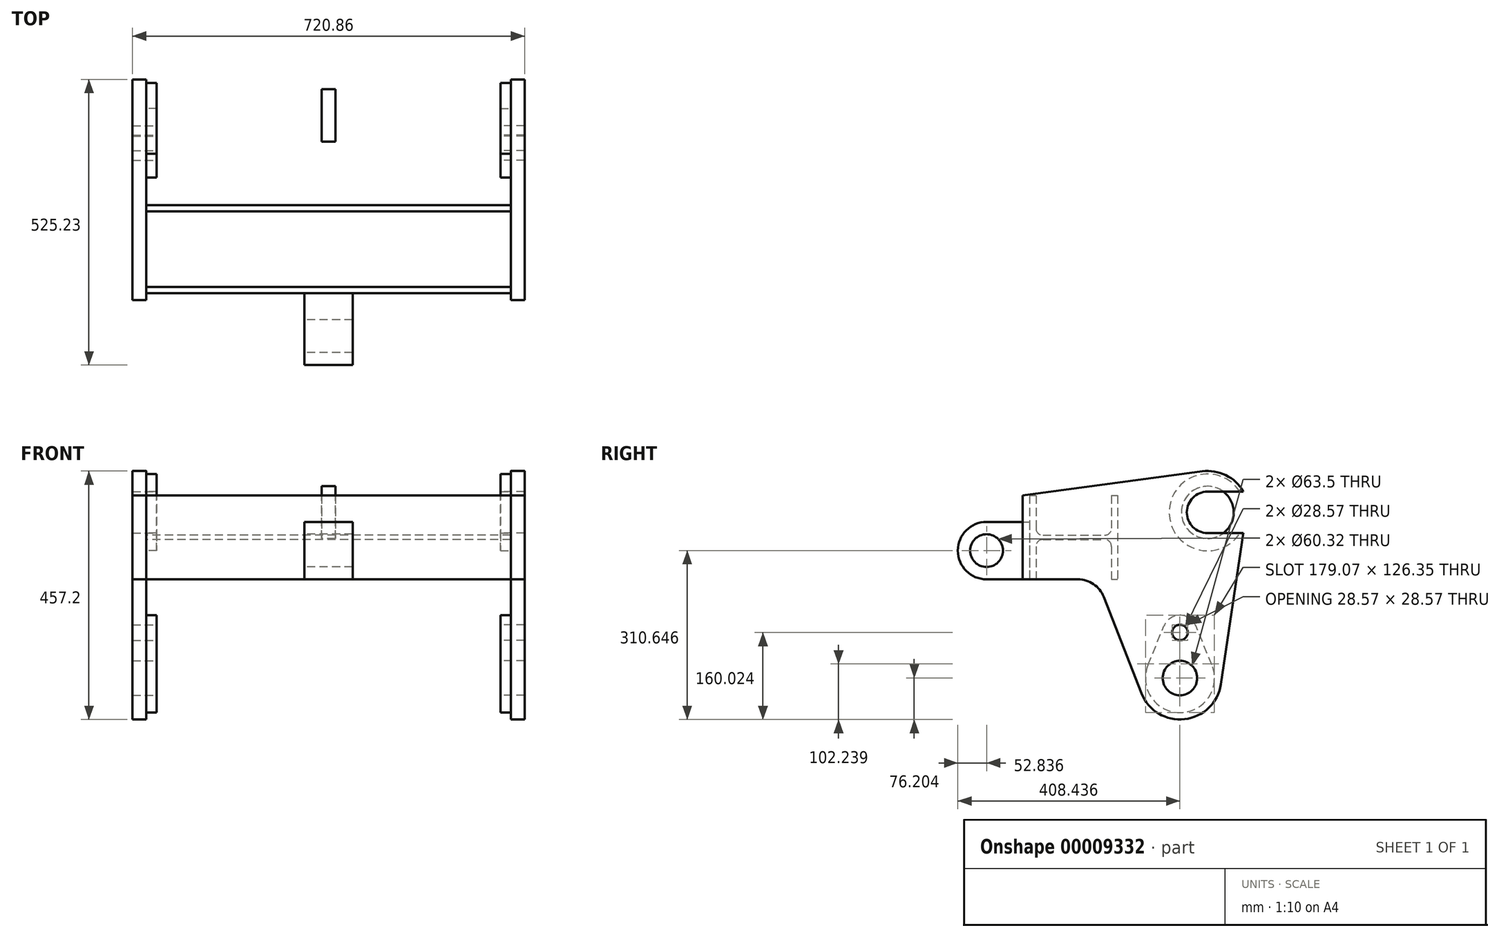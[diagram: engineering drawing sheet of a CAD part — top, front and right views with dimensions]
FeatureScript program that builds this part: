
annotation { "Feature Type Name" : "Feature", "Feature Type Description" : "" }
export const myFeature = defineFeature(function(context is Context, id is Id, definition is map)
    precondition{}
    {
        {
            var Q0;
            Q0=qCreatedBy(makeId("Right.planeOp"),FACE);
            var sketch = newSketch(context, id + "F0", { "sketchPlane" : qUnion([Q0])});
            skLineSegment(sketch, "E0.rect.bottom", {"start": v(-81.03, 77.22) * mm, "end": v(-69.47, 77.22) * mm});
            skLineSegment(sketch, "E0.rect.top", {"start": v(-81.03, -77.22) * mm, "end": v(-69.47, -77.22) * mm});
            skLineSegment(sketch, "E0.rect.left", {"start": v(-81.03, 77.22) * mm, "end": v(-81.03, -77.22) * mm});
            skLineSegment(sketch, "E0.rect.right", {"start": v(81.03, 77.22) * mm, "end": v(81.03, -77.22) * mm});
            skPoint(sketch, "E0.rect.middle", {"position": v(0, 0) * mm});
            skLineSegment(sketch, "E1.0", {"start": v(-69.47, 77.22) * mm, "end": v(-69.47, -77.22) * mm});
            skLineSegment(sketch, "E2", {"start": v(-81.03, 0) * mm, "end": v(81.03, 0) * mm, "construction": true});
            skLineSegment(sketch, "E3", {"start": v(0, 77.22) * mm, "end": v(0, -77.22) * mm, "construction": true});
            skLineSegment(sketch, "E4.0", {"start": v(-81.03, -4.06) * mm, "end": v(81.03, -4.06) * mm});
            skLineSegment(sketch, "E5.0.MirrorCS", {"start": v(-81.03, 4.06) * mm, "end": v(81.03, 4.06) * mm});
            skLineSegment(sketch, "E6.0.MirrorCS", {"start": v(69.47, 77.22) * mm, "end": v(69.47, -77.22) * mm});
            skLineSegment(sketch, "E7.trimOffspring", {"start": v(69.47, 77.22) * mm, "end": v(81.03, 77.22) * mm});
            skLineSegment(sketch, "E8.trimOffspring", {"start": v(69.47, -77.22) * mm, "end": v(81.03, -77.22) * mm});
            skSolve(sketch);
        }
        {
            var Q0;
            Q0 = qSketchRegion(id + "F0", true);
            extrude(context, id + "F1", {"entities" : qUnion([Q0]), "endBound" : BoundingType.SYMMETRIC, "depth" : 670.05 * mm});
        }
        {
            var Q0;
            Q0=makeQuery(id+"F1.opExtrude","SWEPT_EDGE",EDGE,{"disambiguationData":[OSD([sQuery(id+"F0.wireOp",EDGE,"E5.0.MirrorCS"),sQuery(id+"F0.wireOp",EDGE,"E6.0.MirrorCS")])]});
            var Q1;
            Q1=makeQuery(id+"F1.opExtrude","SWEPT_EDGE",EDGE,{"disambiguationData":[OSD([sQuery(id+"F0.wireOp",EDGE,"E4.0"),sQuery(id+"F0.wireOp",EDGE,"E6.0.MirrorCS")])]});
            var Q2;
            Q2=makeQuery(id+"F1.opExtrude","SWEPT_EDGE",EDGE,{"disambiguationData":[OSD([sQuery(id+"F0.wireOp",EDGE,"E1.0"),sQuery(id+"F0.wireOp",EDGE,"E5.0.MirrorCS")])]});
            var Q3;
            Q3=makeQuery(id+"F1.opExtrude","SWEPT_EDGE",EDGE,{"disambiguationData":[OSD([sQuery(id+"F0.wireOp",EDGE,"E1.0"),sQuery(id+"F0.wireOp",EDGE,"E4.0")])]});
            fillet(context, id + "F2", {"entities" : qUnion([Q0, Q1, Q2, Q3]), "radius" : 12.7 * mm, "tangentPropagation" : true, "allowEdgeOverflow" : false});
        }
        {
            var Q0;
            Q0=makeQuery(id+"F1.opExtrude","CAP_FACE",FACE,{"disambiguationData":[OSD([sQuery(id+"F0.wireOp",EDGE,"E0.rect.bottom"),sQuery(id+"F0.wireOp",EDGE,"E0.rect.top"),sQuery(id+"F0.wireOp",EDGE,"E0.rect.left"),sQuery(id+"F0.wireOp",EDGE,"E0.rect.right"),sQuery(id+"F0.wireOp",EDGE,"E1.0"),sQuery(id+"F0.wireOp",EDGE,"E4.0"),sQuery(id+"F0.wireOp",EDGE,"E5.0.MirrorCS"),sQuery(id+"F0.wireOp",EDGE,"E6.0.MirrorCS"),sQuery(id+"F0.wireOp",EDGE,"E7.trimOffspring"),sQuery(id+"F0.wireOp",EDGE,"E8.trimOffspring")])],"isStart":false});
            var sketch = newSketch(context, id + "F3", { "sketchPlane" : qUnion([Q0])});
            skLineSegment(sketch, "E9", {"start": v(-81.03, -4.06) * mm, "end": v(-81.03, 203.68) * mm, "construction": true});
            skLineSegment(sketch, "E10.0", {"start": v(246.13, -4.06) * mm, "end": v(246.13, 203.68) * mm, "construction": true});
            skLineSegment(sketch, "E11", {"start": v(81.03, 0) * mm, "end": v(356.17, 0) * mm, "construction": true});
            skLineSegment(sketch, "E12.0", {"start": v(81.03, 45.97) * mm, "end": v(356.17, 45.97) * mm, "construction": true});
            skArc(sketch, "E13", {"start": v(312.12, 84.07) * mm, "mid": v(279.74, 114.36) * mm, "end": v(235.98, 121.5) * mm});
            skArc(sketch, "E14", {"start": v(246.13, 84.07) * mm, "mid": v(208.03, 45.97) * mm, "end": v(246.13, 7.87) * mm});
            skLineSegment(sketch, "E15", {"start": v(246.13, 84.07) * mm, "end": v(312.12, 84.07) * mm});
            skLineSegment(sketch, "E16", {"start": v(246.13, 7.87) * mm, "end": v(312.12, 7.87) * mm});
            skLineSegment(sketch, "E17.0", {"start": v(81.03, -258.83) * mm, "end": v(356.17, -258.83) * mm, "construction": true});
            skLineSegment(sketch, "E18.0", {"start": v(195.33, -258.83) * mm, "end": v(195.33, 203.68) * mm, "construction": true});
            skCircle(sketch, "E19", {"center": v(195.33, -258.83) * mm, "radius": 31.75 * mm});
            skArc(sketch, "E20", {"start": v(124.35, -286.55) * mm, "mid": v(209.43, -333.7) * mm, "end": v(271.53, -258.83) * mm});
            skLineSegment(sketch, "E21.0", {"start": v(-93.73, 77.22) * mm, "end": v(-93.73, -77.22) * mm});
            skLineSegment(sketch, "E22", {"start": v(-93.73, 77.22) * mm, "end": v(235.98, 121.5) * mm});
            skLineSegment(sketch, "E23.0", {"start": v(7.87, 77.22) * mm, "end": v(7.87, -128.02) * mm, "construction": true});
            skLineSegment(sketch, "E24", {"start": v(-93.73, -77.22) * mm, "end": v(7.87, -77.22) * mm});
            skLineSegment(sketch, "E25.0", {"start": v(-93.73, -128.02) * mm, "end": v(133.5, -128.02) * mm, "construction": true});
            skArc(sketch, "E26", {"start": v(55.2, -109.53) * mm, "mid": v(36.52, -86.07) * mm, "end": v(7.87, -77.22) * mm});
            skLineSegment(sketch, "E27.trimOffspring", {"start": v(113.52, -258.83) * mm, "end": v(124.35, -286.55) * mm});
            skLineSegment(sketch, "E28", {"start": v(113.52, -258.83) * mm, "end": v(55.2, -109.53) * mm});
            skLineSegment(sketch, "E29", {"start": v(312.12, 7.87) * mm, "end": v(270.7, -270.06) * mm});
            skSolve(sketch);
        }
        {
            var Q0;
            Q0 = qSketchRegion(id + "F3", true);
            extrude(context, id + "F4", {"entities" : qUnion([Q0]), "operationType" : NewBodyOperationType.ADD, "depth" : 25.4 * mm});
        }
        {
            var Q0;
            Q0=makeQuery(id+"F4.opExtrude","CAP_FACE",FACE,{"disambiguationData":[OSD([sQuery(id+"F3.wireOp",EDGE,"E13"),sQuery(id+"F3.wireOp",EDGE,"E14"),sQuery(id+"F3.wireOp",EDGE,"E15"),sQuery(id+"F3.wireOp",EDGE,"E16"),sQuery(id+"F3.wireOp",EDGE,"E19"),sQuery(id+"F3.wireOp",EDGE,"E20"),sQuery(id+"F3.wireOp",EDGE,"E21.0"),sQuery(id+"F3.wireOp",EDGE,"E22"),sQuery(id+"F3.wireOp",EDGE,"E24"),sQuery(id+"F3.wireOp",EDGE,"E26"),sQuery(id+"F3.wireOp",EDGE,"E27.trimOffspring"),sQuery(id+"F3.wireOp",EDGE,"E28"),sQuery(id+"F3.wireOp",EDGE,"E29")])],"isStart":true});
            var sketch = newSketch(context, id + "F5", { "sketchPlane" : qUnion([Q0])});
            skArc(sketch, "E30", {"start": v(-254.1, -234.77) * mm, "mid": v(-195.33, -322.33) * mm, "end": v(-136.56, -234.77) * mm});
            skLineSegment(sketch, "E31", {"start": v(-195.33, -258.83) * mm, "end": v(-195.33, -175) * mm, "construction": true});
            skArc(sketch, "E32", {"start": v(-165.94, -162.98) * mm, "mid": v(-195.33, -143.26) * mm, "end": v(-224.71, -162.98) * mm});
            skCircle(sketch, "E33.0", {"center": v(-195.33, -258.83) * mm, "radius": 31.75 * mm});
            skLineSegment(sketch, "E34", {"start": v(-254.1, -234.77) * mm, "end": v(-224.71, -162.98) * mm});
            skLineSegment(sketch, "E35.0.MirrorCS", {"start": v(-136.56, -234.77) * mm, "end": v(-165.94, -162.98) * mm});
            skSolve(sketch);
        }
        {
            var Q0;
            Q0 = qSketchRegion(id + "F5", true);
            extrude(context, id + "F6", {"entities" : qUnion([Q0]), "operationType" : NewBodyOperationType.ADD, "depth" : 19.05 * mm});
        }
        {
            var Q0;
            Q0=makeQuery(id+"F6.opExtrude","CAP_FACE",FACE,{"disambiguationData":[OSD([sQuery(id+"F5.wireOp",EDGE,"E30"),sQuery(id+"F5.wireOp",EDGE,"E32"),sQuery(id+"F5.wireOp",EDGE,"E33.0"),sQuery(id+"F5.wireOp",EDGE,"E34"),sQuery(id+"F5.wireOp",EDGE,"E35.0.MirrorCS")])],"isStart":false});
            var sketch = newSketch(context, id + "F7", { "sketchPlane" : qUnion([Q0])});
            skCircle(sketch, "E36", {"center": v(-195.33, -175) * mm, "radius": 14.29 * mm});
            skSolve(sketch);
        }
        {
            var Q0;
            Q0 = qSketchRegion(id + "F7", true);
            extrude(context, id + "F8", {"entities" : qUnion([Q0]), "operationType" : NewBodyOperationType.REMOVE, "endBound" : BoundingType.THROUGH_ALL, "oppositeDirection" : true, "depth" : 25.4 * mm});
        }
        {
            var Q0;
            Q0=makeQuery(id+"F4.opExtrude","CAP_FACE",FACE,{"disambiguationData":[OSD([sQuery(id+"F3.wireOp",EDGE,"E13"),sQuery(id+"F3.wireOp",EDGE,"E14"),sQuery(id+"F3.wireOp",EDGE,"E15"),sQuery(id+"F3.wireOp",EDGE,"E16"),sQuery(id+"F3.wireOp",EDGE,"E19"),sQuery(id+"F3.wireOp",EDGE,"E20"),sQuery(id+"F3.wireOp",EDGE,"E21.0"),sQuery(id+"F3.wireOp",EDGE,"E22"),sQuery(id+"F3.wireOp",EDGE,"E24"),sQuery(id+"F3.wireOp",EDGE,"E26"),sQuery(id+"F3.wireOp",EDGE,"E27.trimOffspring"),sQuery(id+"F3.wireOp",EDGE,"E28"),sQuery(id+"F3.wireOp",EDGE,"E29")])],"isStart":true});
            var sketch = newSketch(context, id + "F9", { "sketchPlane" : qUnion([Q0])});
            skArc(sketch, "E37", {"start": v(-305.64, 7.87) * mm, "mid": v(-175.46, 45.97) * mm, "end": v(-305.64, 84.07) * mm});
            skLineSegment(sketch, "E38.0", {"start": v(-246.13, 84.07) * mm, "end": v(-312.12, 84.07) * mm});
            skArc(sketch, "E39.0", {"start": v(-246.13, 84.07) * mm, "mid": v(-208.03, 45.97) * mm, "end": v(-246.13, 7.87) * mm});
            skLineSegment(sketch, "E40.0", {"start": v(-246.13, 7.87) * mm, "end": v(-312.12, 7.87) * mm});
            skSolve(sketch);
        }
        {
            var Q0;
            Q0 = qSketchRegion(id + "F9", true);
            extrude(context, id + "F10", {"entities" : qUnion([Q0]), "operationType" : NewBodyOperationType.ADD, "depth" : 19.05 * mm});
        }
        {
            var Q0;
            Q0=qCreatedBy(makeId("Right.planeOp"),FACE);
            var sketch = newSketch(context, id + "F11", { "sketchPlane" : qUnion([Q0])});
            skLineSegment(sketch, "E41.0", {"start": v(-160.27, 77.22) * mm, "end": v(-160.27, -77.22) * mm, "construction": true});
            skLineSegment(sketch, "E42.0", {"start": v(-81.03, 77.22) * mm, "end": v(-81.03, -77.22) * mm, "construction": true});
            skLineSegment(sketch, "E43", {"start": v(-81.03, 77.22) * mm, "end": v(-252.94, 77.22) * mm, "construction": true});
            skLineSegment(sketch, "E44.0", {"start": v(-81.03, -24.38) * mm, "end": v(-252.94, -24.38) * mm, "construction": true});
            skArc(sketch, "E45", {"start": v(-160.27, 28.45) * mm, "mid": v(-213.1, -24.38) * mm, "end": v(-160.27, -77.22) * mm});
            skCircle(sketch, "E46", {"center": v(-160.27, -24.38) * mm, "radius": 30.16 * mm});
            skLineSegment(sketch, "E47", {"start": v(-160.27, 28.45) * mm, "end": v(-81.03, 28.45) * mm});
            skLineSegment(sketch, "E48", {"start": v(-81.03, 28.45) * mm, "end": v(-81.03, -77.22) * mm});
            skLineSegment(sketch, "E49", {"start": v(-160.27, -77.22) * mm, "end": v(-81.03, -77.22) * mm});
            skSolve(sketch);
        }
        {
            var Q0;
            Q0 = qSketchRegion(id + "F11", true);
            extrude(context, id + "F12", {"entities" : qUnion([Q0]), "operationType" : NewBodyOperationType.ADD, "endBound" : BoundingType.SYMMETRIC, "depth" : 88.9 * mm});
        }
        {
            var Q0;
            Q0=makeQuery(id+"F1.opExtrude","SWEPT_BODY",BODY,{"disambiguationData":[OSD([sQuery(id+"F0.wireOp",EDGE,"E0.rect.bottom"),sQuery(id+"F0.wireOp",EDGE,"E0.rect.top"),sQuery(id+"F0.wireOp",EDGE,"E0.rect.left"),sQuery(id+"F0.wireOp",EDGE,"E0.rect.right"),sQuery(id+"F0.wireOp",EDGE,"E1.0"),sQuery(id+"F0.wireOp",EDGE,"E4.0"),sQuery(id+"F0.wireOp",EDGE,"E5.0.MirrorCS"),sQuery(id+"F0.wireOp",EDGE,"E6.0.MirrorCS"),sQuery(id+"F0.wireOp",EDGE,"E7.trimOffspring"),sQuery(id+"F0.wireOp",EDGE,"E8.trimOffspring")])]});
            var Q1;
            Q1=qCreatedBy(makeId("Right.planeOp"),FACE);
            mirror(context, id + "F13", {"entities" : qUnion([Q0]), "mirrorPlane" : qUnion([Q1])});
        }
        {
            var Q0;
            Q0=qCreatedBy(makeId("Right.planeOp"),FACE);
            var sketch = newSketch(context, id + "F14", { "sketchPlane" : qUnion([Q0])});
            skArc(sketch, "E50.0", {"start": v(246.13, 84.07) * mm, "mid": v(208.03, 45.97) * mm, "end": v(246.13, 7.87) * mm, "construction": true});
            skCircle(sketch, "E51", {"center": v(246.13, 45.97) * mm, "radius": 48.05 * mm});
            skSolve(sketch);
        }
        {
            var Q0;
            Q0 = qSketchRegion(id + "F14", true);
            extrude(context, id + "F15", {"entities" : qUnion([Q0]), "endBound" : BoundingType.SYMMETRIC, "depth" : 25.4 * mm});
        }
    });
